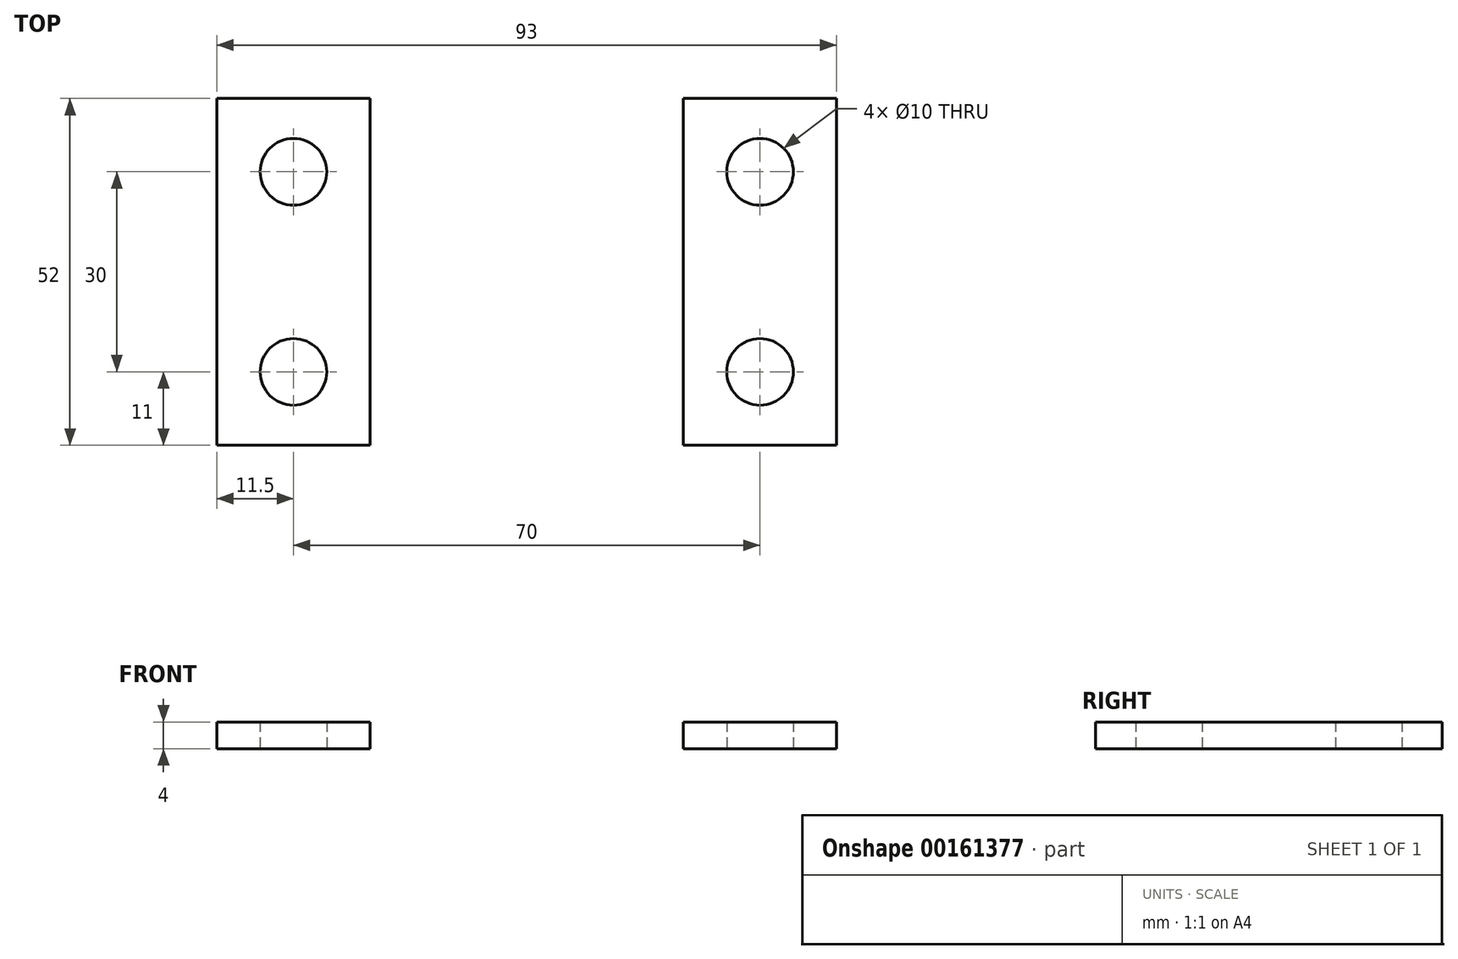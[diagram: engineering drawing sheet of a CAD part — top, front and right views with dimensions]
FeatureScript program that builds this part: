
annotation { "Feature Type Name" : "Feature", "Feature Type Description" : "" }
export const myFeature = defineFeature(function(context is Context, id is Id, definition is map)
    precondition{}
    {
        {
            var Q0;
            Q0=qCreatedBy(makeId("Top.planeOp"),FACE);
            var sketch = newSketch(context, id + "F0", { "sketchPlane" : qUnion([Q0])});
            skLineSegment(sketch, "E0.bottom", {"start": v(11.5, 26) * mm, "end": v(-11.5, 26) * mm});
            skLineSegment(sketch, "E0.top", {"start": v(11.5, -26) * mm, "end": v(-11.5, -26) * mm});
            skLineSegment(sketch, "E0.left", {"start": v(11.5, 26) * mm, "end": v(11.5, -26) * mm});
            skLineSegment(sketch, "E0.right", {"start": v(-11.5, 26) * mm, "end": v(-11.5, -26) * mm});
            skPoint(sketch, "E0.middle", {"position": v(0, 0) * mm});
            skPoint(sketch, "E1", {"position": v(0, 15) * mm});
            skPoint(sketch, "E1.positionSnap0", {"position": v(0, 26) * mm});
            skPoint(sketch, "E2", {"position": v(0, -15) * mm});
            skPoint(sketch, "E2.positionSnap0", {"position": v(0, -26) * mm});
            skCircle(sketch, "E3", {"center": v(0, -15) * mm, "radius": 5 * mm});
            skCircle(sketch, "E4", {"center": v(0, 15) * mm, "radius": 5 * mm});
            skPoint(sketch, "E5.MirrorP", {"position": v(70, -15) * mm});
            skPoint(sketch, "E6.MirrorP", {"position": v(70, 26) * mm});
            skPoint(sketch, "E7.MirrorP", {"position": v(70, 15) * mm});
            skLineSegment(sketch, "E8.MirrorCS", {"start": v(58.5, 26) * mm, "end": v(81.5, 26) * mm});
            skLineSegment(sketch, "E9.MirrorCS", {"start": v(58.5, -26) * mm, "end": v(81.5, -26) * mm});
            skCircle(sketch, "E10.MirrorC", {"center": v(70, 15) * mm, "radius": 5 * mm});
            skCircle(sketch, "E11.MirrorC", {"center": v(70, -15) * mm, "radius": 5 * mm});
            skLineSegment(sketch, "E12.MirrorCS", {"start": v(58.5, 26) * mm, "end": v(58.5, -26) * mm});
            skLineSegment(sketch, "E13.MirrorCS", {"start": v(81.5, 26) * mm, "end": v(81.5, -26) * mm});
            skPoint(sketch, "E14.MirrorP", {"position": v(70, 0) * mm});
            skPoint(sketch, "E15.MirrorP", {"position": v(70, -26) * mm});
            skSolve(sketch);
        }
        {
            var Q0;
            Q0=makeQuery(id+"F0.imprint","IMPRINT",FACE,{"disambiguationData":[TD([[makeQuery(id+"F0.imprint","IMPRINT",EDGE,{"derivedFrom":sQuery(id+"F0.wireOp",EDGE,"E8.MirrorCS")}),-1.0]])]});
            var Q1;
            Q1=makeQuery(id+"F0.imprint","IMPRINT",FACE,{"disambiguationData":[TD([[makeQuery(id+"F0.imprint","IMPRINT",EDGE,{"derivedFrom":sQuery(id+"F0.wireOp",EDGE,"E0.bottom")}),1.0]])]});
            extrude(context, id + "F1", {"entities" : qUnion([Q0, Q1]), "depth" : 4 * mm});
        }
    });
